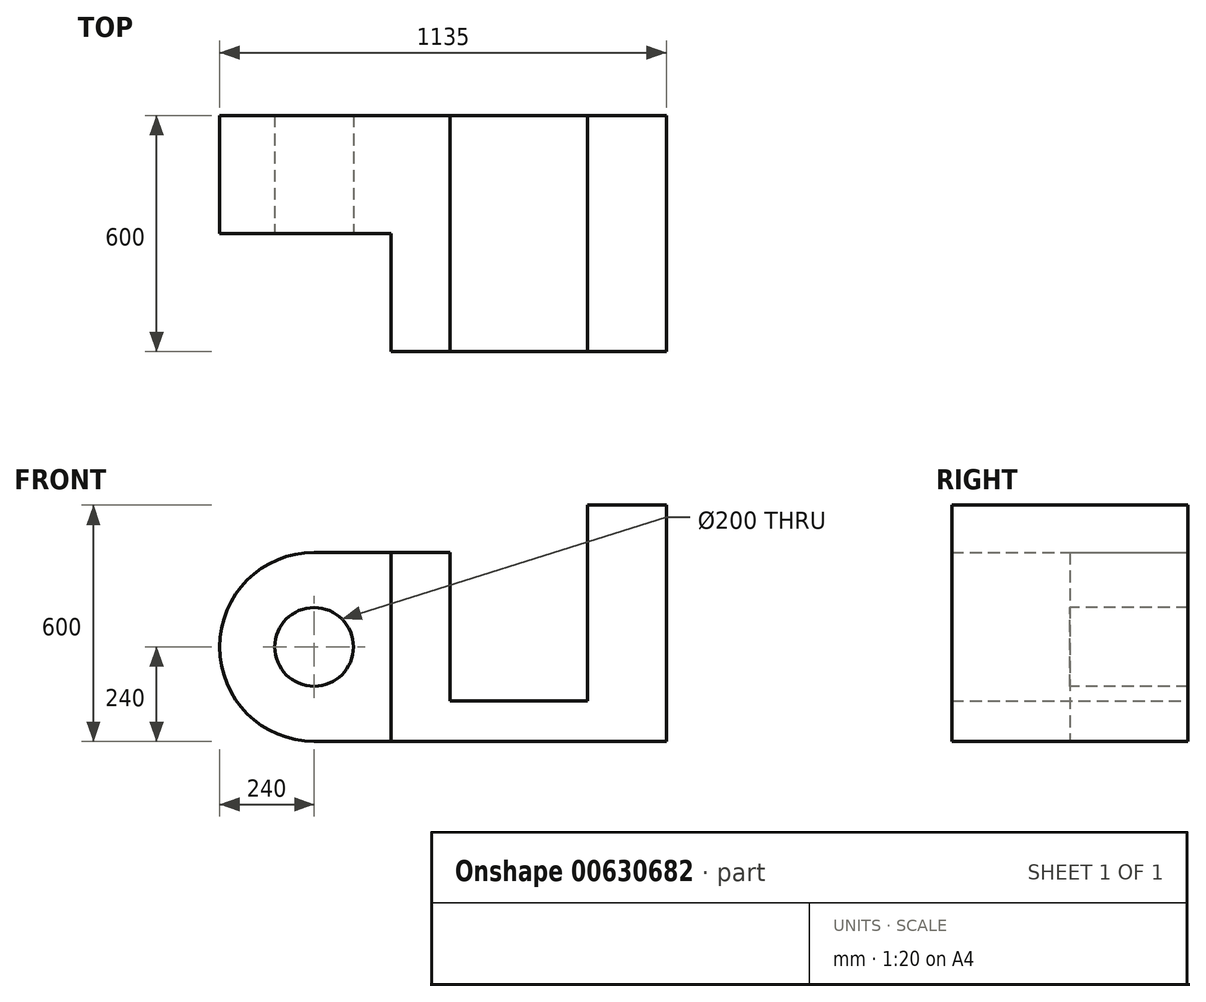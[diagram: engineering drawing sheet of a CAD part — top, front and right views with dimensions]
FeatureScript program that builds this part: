
annotation { "Feature Type Name" : "Feature", "Feature Type Description" : "" }
export const myFeature = defineFeature(function(context is Context, id is Id, definition is map)
    precondition{}
    {
        {
            var Q0;
            Q0=qCreatedBy(makeId("Front.planeOp"),FACE);
            var sketch = newSketch(context, id + "F0", { "sketchPlane" : qUnion([Q0])});
            skLineSegment(sketch, "E0.bottom", {"start": v(-350, -300) * mm, "end": v(350, -300) * mm});
            skLineSegment(sketch, "E0.top", {"start": v(-350, 300) * mm, "end": v(350, 300) * mm});
            skLineSegment(sketch, "E0.left", {"start": v(-350, -300) * mm, "end": v(-350, 300) * mm});
            skLineSegment(sketch, "E0.right", {"start": v(350, -300) * mm, "end": v(350, 300) * mm});
            skPoint(sketch, "E0.middle", {"position": v(0, 0) * mm});
            skLineSegment(sketch, "E1", {"start": v(150, 300) * mm, "end": v(150, -196.9) * mm});
            skLineSegment(sketch, "E2", {"start": v(150, -196.9) * mm, "end": v(-200, -196.9) * mm});
            skLineSegment(sketch, "E3", {"start": v(-200, -196.9) * mm, "end": v(-200, 180) * mm});
            skLineSegment(sketch, "E4", {"start": v(-200, 180) * mm, "end": v(-350, 180) * mm});
            skSolve(sketch);
        }
        {
            var Q0;
            {var subQ1=sQuery(id+"F0.wireOp",EDGE,"E0.bottom");Q0=makeQuery(id+"F0.imprint","IMPRINT",FACE,{"disambiguationData":[TD([[makeQuery(id+"F0.imprint","IMPRINT",EDGE,{"derivedFrom":subQ1}),1.0]])]});}
            extrude(context, id + "F1", {"entities" : qUnion([Q0]), "depth" : 600 * mm, "offsetDistance" : 25 * mm});
        }
        {
            var Q0;
            Q0=makeQuery(id+"F1.opExtrude","SWEPT_FACE",FACE,{"disambiguationData":[OSD([sQuery(id+"F0.wireOp",EDGE,"E0.left")])]});
            var sketch = newSketch(context, id + "F2", { "sketchPlane" : qUnion([Q0])});
            skLineSegment(sketch, "E5.bottom", {"start": v(300, 180) * mm, "end": v(0, 180) * mm});
            skLineSegment(sketch, "E5.top", {"start": v(300, -300) * mm, "end": v(0, -300) * mm});
            skLineSegment(sketch, "E5.left", {"start": v(300, 180) * mm, "end": v(300, -300) * mm});
            skLineSegment(sketch, "E5.right", {"start": v(0, 180) * mm, "end": v(0, -300) * mm});
            skSolve(sketch);
        }
        {
            var Q0;
            Q0 = qSketchRegion(id + "F2", true);
            extrude(context, id + "F3", {"entities" : qUnion([Q0]), "operationType" : NewBodyOperationType.ADD, "depth" : 195 * mm, "offsetDistance" : 25 * mm});
        }
        {
            var Q0;
            Q0=makeQuery(id+"F3.opExtrude","SWEPT_FACE",FACE,{"disambiguationData":[OSD([sQuery(id+"F2.wireOp",EDGE,"E5.left")])]});
            var sketch = newSketch(context, id + "F4", { "sketchPlane" : qUnion([Q0])});
            skCircle(sketch, "E6", {"center": v(-545, -60) * mm, "radius": 240 * mm});
            skLineSegment(sketch, "E7", {"start": v(-545, 180) * mm, "end": v(-545, -300) * mm});
            skSolve(sketch);
        }
        {
            var Q0;
            Q0 = qSketchRegion(id + "F4", true);
            extrude(context, id + "F5", {"entities" : qUnion([Q0]), "operationType" : NewBodyOperationType.ADD, "oppositeDirection" : true, "depth" : 300 * mm, "offsetDistance" : 25 * mm});
        }
        {
            var Q0;
            Q0=makeQuery(id+"F5.boolean.opBoolean","MERGE",FACE,{"derivedFrom":[makeQuery(id+"F3.opExtrude","SWEPT_FACE",FACE,{"disambiguationData":[OSD([sQuery(id+"F2.wireOp",EDGE,"E5.left")])]}),makeQuery(id+"F5.opExtrude","CAP_FACE",FACE,{"disambiguationData":[OSD([sQuery(id+"F4.wireOp",EDGE,"E6")])],"isStart":true})]});
            var sketch = newSketch(context, id + "F6", { "sketchPlane" : qUnion([Q0])});
            skCircle(sketch, "E8", {"center": v(-545, -60) * mm, "radius": 100 * mm});
            skSolve(sketch);
        }
        {
            var Q0;
            Q0 = qSketchRegion(id + "F6", true);
            extrude(context, id + "F7", {"entities" : qUnion([Q0]), "operationType" : NewBodyOperationType.REMOVE, "endBound" : BoundingType.THROUGH_ALL, "oppositeDirection" : true, "depth" : 25 * mm, "offsetDistance" : 25 * mm});
        }
    });
